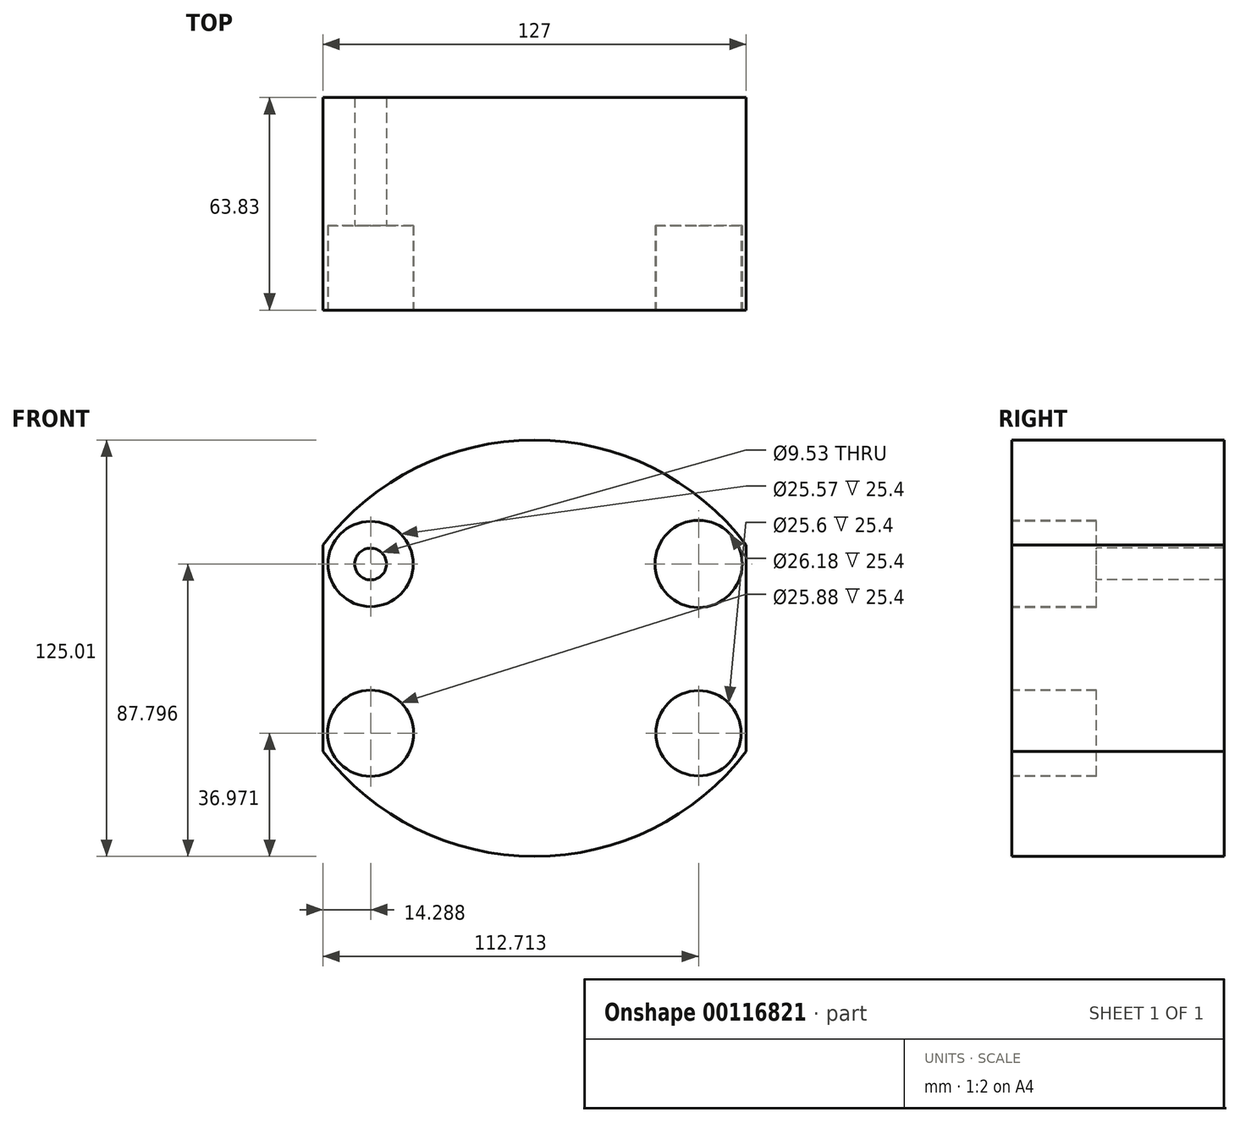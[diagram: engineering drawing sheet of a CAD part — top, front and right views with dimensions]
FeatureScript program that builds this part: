
annotation { "Feature Type Name" : "Feature", "Feature Type Description" : "" }
export const myFeature = defineFeature(function(context is Context, id is Id, definition is map)
    precondition{}
    {
        {
            var Q0;
            Q0=qCreatedBy(makeId("Front.planeOp"),FACE);
            var sketch = newSketch(context, id + "F0", { "sketchPlane" : qUnion([Q0])});
            skLineSegment(sketch, "E0.bottom", {"start": v(-63.5, 31) * mm, "end": v(63.5, 31) * mm});
            skLineSegment(sketch, "E0.top", {"start": v(-63.5, -31) * mm, "end": v(63.5, -31) * mm});
            skLineSegment(sketch, "E0.left", {"start": v(-63.5, 31) * mm, "end": v(-63.5, -31) * mm});
            skLineSegment(sketch, "E0.right", {"start": v(63.5, 31) * mm, "end": v(63.5, -31) * mm});
            skPoint(sketch, "E0.middle", {"position": v(0, 0) * mm});
            skLineSegment(sketch, "E1", {"start": v(0, 0) * mm, "end": v(0, -62.5) * mm});
            skLineSegment(sketch, "E2", {"start": v(0, -62.5) * mm, "end": v(0, 0) * mm});
            skLineSegment(sketch, "E3", {"start": v(0, 0) * mm, "end": v(0, 62.5) * mm});
            skLineSegment(sketch, "E4", {"start": v(0, 62.5) * mm, "end": v(0, 0) * mm});
            skArc(sketch, "E5", {"start": v(63.5, 31) * mm, "mid": v(0, 62.5) * mm, "end": v(-63.5, 31) * mm});
            skArc(sketch, "E6", {"start": v(-63.5, -31) * mm, "mid": v(0, -62.5) * mm, "end": v(63.5, -31) * mm});
            skSolve(sketch);
        }
        {
            var Q0;
            Q0=qSketchRegion(id+"F0",true);
            extrude(context, id + "F1", {"entities" : qUnion([Q0]), "depth" : 104.5 * mm});
        }
        {
            var Q0;
            Q0=makeQuery(id+"F1.opExtrude","SWEPT_FACE",FACE,{"disambiguationData":[OSD([sQuery(id+"F0.wireOp",EDGE,"E0.right")])]});
            var sketch = newSketch(context, id + "F2", { "sketchPlane" : qUnion([Q0])});
            skLineSegment(sketch, "E7.bottom", {"start": v(-104.5, 31) * mm, "end": v(-62.5, 31) * mm});
            skLineSegment(sketch, "E7.top", {"start": v(-104.5, -31) * mm, "end": v(-62.5, -31) * mm});
            skLineSegment(sketch, "E7.left", {"start": v(-104.5, 31) * mm, "end": v(-104.5, -31) * mm});
            skLineSegment(sketch, "E7.right", {"start": v(-62.5, 31) * mm, "end": v(-62.5, -31) * mm});
            skLineSegment(sketch, "E8", {"start": v(-62.5, 31) * mm, "end": v(-62.5, 64.33) * mm});
            skLineSegment(sketch, "E9", {"start": v(-62.5, 64.33) * mm, "end": v(-104.5, 31) * mm});
            skLineSegment(sketch, "E10", {"start": v(-62.5, -31) * mm, "end": v(-62.5, -65.1) * mm});
            skLineSegment(sketch, "E11", {"start": v(-62.5, -65.1) * mm, "end": v(-104.5, -31) * mm});
            skLineSegment(sketch, "E12", {"start": v(-104.5, -31) * mm, "end": v(-104.5, -67.31) * mm});
            skLineSegment(sketch, "E13", {"start": v(-104.5, -67.31) * mm, "end": v(-62.5, -65.1) * mm});
            skLineSegment(sketch, "E14", {"start": v(-104.5, 31) * mm, "end": v(-104.5, 72.84) * mm});
            skLineSegment(sketch, "E15", {"start": v(-104.5, 72.84) * mm, "end": v(-62.5, 64.33) * mm});
            skSolve(sketch);
        }
        {
            var Q0;
            Q0=makeQuery(id+"F2.imprint","IMPRINT",FACE,{"disambiguationData":[TD([[makeQuery(id+"F2.imprint","IMPRINT",EDGE,{"derivedFrom":sQuery(id+"F2.wireOp",EDGE,"E9")}),-1.0]])]});
            var Q1;
            Q1=makeQuery(id+"F2.imprint","IMPRINT",FACE,{"disambiguationData":[TD([[makeQuery(id+"F2.imprint","IMPRINT",EDGE,{"derivedFrom":sQuery(id+"F2.wireOp",EDGE,"E11")}),1.0]])]});
            extrude(context, id + "F3", {"entities" : qUnion([Q0, Q1]), "operationType" : NewBodyOperationType.REMOVE, "endBound" : BoundingType.THROUGH_ALL, "oppositeDirection" : true, "depth" : 25.4 * mm});
        }
        {
            var Q0;
            Q0=makeQuery(id+"F1.opExtrude","CAP_FACE",FACE,{"disambiguationData":[OSD([sQuery(id+"F0.wireOp",EDGE,"E0.left"),sQuery(id+"F0.wireOp",EDGE,"E0.right"),sQuery(id+"F0.wireOp",EDGE,"E5"),sQuery(id+"F0.wireOp",EDGE,"E6")])],"isStart":false});
            var sketch = newSketch(context, id + "F4", { "sketchPlane" : qUnion([Q0])});
            skLineSegment(sketch, "E16.bottom", {"start": v(-63.5, 31) * mm, "end": v(63.5, 31) * mm});
            skLineSegment(sketch, "E16.top", {"start": v(-63.5, -31) * mm, "end": v(63.5, -31) * mm});
            skLineSegment(sketch, "E16.left", {"start": v(-63.5, 31) * mm, "end": v(-63.5, -31) * mm});
            skLineSegment(sketch, "E16.right", {"start": v(63.5, 31) * mm, "end": v(63.5, -31) * mm});
            skSolve(sketch);
        }
        {
            var Q0;
            Q0=qSketchRegion(id+"F4",true);
            extrude(context, id + "F5", {"entities" : qUnion([Q0]), "operationType" : NewBodyOperationType.ADD, "depth" : 27 * mm});
        }
        {
            var Q0;
            Q0=makeQuery(id+"F5.opExtrude","SWEPT_FACE",FACE,{"disambiguationData":[OSD([sQuery(id+"F4.wireOp",EDGE,"E16.top")])]});
            var sketch = newSketch(context, id + "F6", { "sketchPlane" : qUnion([Q0])});
            skPoint(sketch, "E17", {"position": v(0, 131.5) * mm});
            skArc(sketch, "E18", {"start": v(63.5, 104.5) * mm, "mid": v(0, 131.5) * mm, "end": v(-63.5, 104.5) * mm});
            skLineSegment(sketch, "E19.bottom", {"start": v(-63.5, 131.5) * mm, "end": v(63.5, 131.5) * mm});
            skLineSegment(sketch, "E19.top", {"start": v(-63.5, 104.5) * mm, "end": v(63.5, 104.5) * mm});
            skLineSegment(sketch, "E19.left", {"start": v(-63.5, 131.5) * mm, "end": v(-63.5, 104.5) * mm});
            skLineSegment(sketch, "E19.right", {"start": v(63.5, 131.5) * mm, "end": v(63.5, 104.5) * mm});
            skSolve(sketch);
        }
        {
            var Q0;
            {var subQ0=sQuery(id+"F6.wireOp",EDGE,"E19.left");Q0=makeQuery(id+"F6.imprint","IMPRINT",FACE,{"disambiguationData":[TD([[makeQuery(id+"F6.imprint","IMPRINT",EDGE,{"derivedFrom":subQ0}),1.0]])]});}
            var Q1;
            {var subQ0=sQuery(id+"F6.wireOp",EDGE,"E19.right");Q1=makeQuery(id+"F6.imprint","IMPRINT",FACE,{"disambiguationData":[TD([[makeQuery(id+"F6.imprint","IMPRINT",EDGE,{"derivedFrom":subQ0}),-1.0]])]});}
            extrude(context, id + "F7", {"entities" : qUnion([Q0, Q1]), "operationType" : NewBodyOperationType.REMOVE, "endBound" : BoundingType.THROUGH_ALL, "oppositeDirection" : true, "depth" : 25.4 * mm});
        }
        {
            var Q0;
            Q0=makeQuery(id+"F5.boolean.opBoolean","MERGE",FACE,{"derivedFrom":[makeQuery(id+"F1.opExtrude","SWEPT_FACE",FACE,{"disambiguationData":[OSD([sQuery(id+"F0.wireOp",EDGE,"E0.right")])]}),makeQuery(id+"F5.opExtrude","SWEPT_FACE",FACE,{"disambiguationData":[OSD([sQuery(id+"F4.wireOp",EDGE,"E16.right")])]})]});
            var sketch = newSketch(context, id + "F8", { "sketchPlane" : qUnion([Q0])});
            skLineSegment(sketch, "E20.bottom", {"start": v(-142.12, -108.78) * mm, "end": v(-63.83, -108.78) * mm});
            skLineSegment(sketch, "E20.top", {"start": v(-142.12, 98.37) * mm, "end": v(-63.83, 98.37) * mm});
            skLineSegment(sketch, "E20.left", {"start": v(-142.12, -108.78) * mm, "end": v(-142.12, 98.37) * mm});
            skLineSegment(sketch, "E20.right", {"start": v(-63.83, -108.78) * mm, "end": v(-63.83, 98.37) * mm});
            skSolve(sketch);
        }
        {
            var Q0;
            Q0 = qSketchRegion(id + "F8", true);
            extrude(context, id + "F9", {"entities" : qUnion([Q0]), "operationType" : NewBodyOperationType.REMOVE, "endBound" : BoundingType.THROUGH_ALL, "oppositeDirection" : true, "depth" : 25.4 * mm});
        }
        {
            var Q0;
            Q0=makeQuery(id+"F9.boolean.opBoolean","COPY",FACE,{"derivedFrom":makeQuery(id+"F9.opExtrude","SWEPT_FACE",FACE,{"disambiguationData":[OSD([sQuery(id+"F8.wireOp",EDGE,"E20.right")])]})});
            var sketch = newSketch(context, id + "F10", { "sketchPlane" : qUnion([Q0])});
            skLineSegment(sketch, "E21", {"start": v(0, 0) * mm, "end": v(-49.21, 0) * mm});
            skLineSegment(sketch, "E22", {"start": v(-49.21, 0) * mm, "end": v(0, 0) * mm});
            skLineSegment(sketch, "E23", {"start": v(0, 0) * mm, "end": v(49.21, 0) * mm});
            skLineSegment(sketch, "E24", {"start": v(49.21, 0) * mm, "end": v(0, 0) * mm});
            skLineSegment(sketch, "E25", {"start": v(49.21, 0) * mm, "end": v(49.21, -25.53) * mm});
            skLineSegment(sketch, "E26", {"start": v(49.21, -25.53) * mm, "end": v(49.21, 25.3) * mm});
            skLineSegment(sketch, "E27", {"start": v(49.21, 25.3) * mm, "end": v(49.21, -25.53) * mm});
            skLineSegment(sketch, "E28", {"start": v(-49.21, 0) * mm, "end": v(-49.21, -25.53) * mm});
            skLineSegment(sketch, "E29", {"start": v(-49.21, -25.53) * mm, "end": v(-49.21, 25.3) * mm});
            skLineSegment(sketch, "E30", {"start": v(-49.21, 25.3) * mm, "end": v(49.21, 25.3) * mm});
            skLineSegment(sketch, "E31", {"start": v(49.21, -25.53) * mm, "end": v(-49.21, -25.53) * mm});
            skCircle(sketch, "E32", {"center": v(49.21, -25.53) * mm, "radius": 4.76 * mm});
            skCircle(sketch, "E33", {"center": v(-49.21, -25.53) * mm, "radius": 4.76 * mm});
            skCircle(sketch, "E34", {"center": v(49.21, 25.3) * mm, "radius": 4.76 * mm});
            skCircle(sketch, "E35", {"center": v(-49.21, 25.3) * mm, "radius": 4.76 * mm});
            skSolve(sketch);
        }
        {
            var Q0;
            {var subQ0=sQuery(id+"F10.wireOp",EDGE,"E31");var subQ1=sQuery(id+"F10.wireOp",EDGE,"E27");var subQ2=makeQuery(id+"F10.imprint","INTERSECT",VERTEX,{"derivedFrom":[subQ1,subQ0]});Q0=makeQuery(id+"F10.imprint","IMPRINT",FACE,{"disambiguationData":[TD([[makeQuery(id+"F10.imprint","IMPRINT",EDGE,{"disambiguationData":[TD([[subQ2,1.0]])],"derivedFrom":subQ1}),1.0]])]});}
            var Q1;
            {var subQ0=sQuery(id+"F10.wireOp",EDGE,"E31");var subQ1=sQuery(id+"F10.wireOp",EDGE,"E27");var subQ2=makeQuery(id+"F10.imprint","INTERSECT",VERTEX,{"derivedFrom":[subQ1,subQ0]});Q1=makeQuery(id+"F10.imprint","IMPRINT",FACE,{"disambiguationData":[TD([[makeQuery(id+"F10.imprint","IMPRINT",EDGE,{"disambiguationData":[TD([[subQ2,1.0]])],"derivedFrom":subQ1}),-1.0]])]});}
            var Q2;
            {var subQ0=sQuery(id+"F10.wireOp",EDGE,"E31");var subQ1=sQuery(id+"F10.wireOp",EDGE,"E29");var subQ2=makeQuery(id+"F10.imprint","INTERSECT",VERTEX,{"derivedFrom":[subQ1,subQ0]});Q2=makeQuery(id+"F10.imprint","IMPRINT",FACE,{"disambiguationData":[TD([[makeQuery(id+"F10.imprint","IMPRINT",EDGE,{"disambiguationData":[TD([[subQ2,-1.0]])],"derivedFrom":subQ1}),-1.0]])]});}
            var Q3;
            {var subQ0=sQuery(id+"F10.wireOp",EDGE,"E31");var subQ1=sQuery(id+"F10.wireOp",EDGE,"E29");var subQ2=makeQuery(id+"F10.imprint","INTERSECT",VERTEX,{"derivedFrom":[subQ1,subQ0]});Q3=makeQuery(id+"F10.imprint","IMPRINT",FACE,{"disambiguationData":[TD([[makeQuery(id+"F10.imprint","IMPRINT",EDGE,{"disambiguationData":[TD([[subQ2,-1.0]])],"derivedFrom":subQ1}),1.0]])]});}
            var Q4;
            {var subQ0=sQuery(id+"F10.wireOp",EDGE,"E30");var subQ1=sQuery(id+"F10.wireOp",EDGE,"E29");var subQ2=makeQuery(id+"F10.imprint","INTERSECT",VERTEX,{"derivedFrom":[subQ1,subQ0]});Q4=makeQuery(id+"F10.imprint","IMPRINT",FACE,{"disambiguationData":[TD([[makeQuery(id+"F10.imprint","IMPRINT",EDGE,{"disambiguationData":[TD([[subQ2,1.0]])],"derivedFrom":subQ1}),1.0]])]});}
            var Q5;
            {var subQ0=sQuery(id+"F10.wireOp",EDGE,"E30");var subQ1=sQuery(id+"F10.wireOp",EDGE,"E29");var subQ2=makeQuery(id+"F10.imprint","INTERSECT",VERTEX,{"derivedFrom":[subQ1,subQ0]});Q5=makeQuery(id+"F10.imprint","IMPRINT",FACE,{"disambiguationData":[TD([[makeQuery(id+"F10.imprint","IMPRINT",EDGE,{"disambiguationData":[TD([[subQ2,1.0]])],"derivedFrom":subQ1}),-1.0]])]});}
            var Q6;
            {var subQ0=sQuery(id+"F10.wireOp",EDGE,"E30");var subQ1=sQuery(id+"F10.wireOp",EDGE,"E27");var subQ2=makeQuery(id+"F10.imprint","INTERSECT",VERTEX,{"derivedFrom":[subQ1,subQ0]});Q6=makeQuery(id+"F10.imprint","IMPRINT",FACE,{"disambiguationData":[TD([[makeQuery(id+"F10.imprint","IMPRINT",EDGE,{"disambiguationData":[TD([[subQ2,-1.0]])],"derivedFrom":subQ1}),1.0]])]});}
            var Q7;
            {var subQ0=sQuery(id+"F10.wireOp",EDGE,"E30");var subQ1=sQuery(id+"F10.wireOp",EDGE,"E27");var subQ2=makeQuery(id+"F10.imprint","INTERSECT",VERTEX,{"derivedFrom":[subQ1,subQ0]});Q7=makeQuery(id+"F10.imprint","IMPRINT",FACE,{"disambiguationData":[TD([[makeQuery(id+"F10.imprint","IMPRINT",EDGE,{"disambiguationData":[TD([[subQ2,-1.0]])],"derivedFrom":subQ1}),-1.0]])]});}
            extrude(context, id + "F11", {"entities" : qUnion([Q0, Q1, Q2, Q3, Q4, Q5, Q6, Q7]), "operationType" : NewBodyOperationType.REMOVE, "endBound" : BoundingType.THROUGH_ALL, "oppositeDirection" : true, "depth" : 25.4 * mm});
        }
        {
            var Q0;
            Q0=makeQuery(id+"F9.boolean.opBoolean","COPY",FACE,{"derivedFrom":makeQuery(id+"F9.opExtrude","SWEPT_FACE",FACE,{"disambiguationData":[OSD([sQuery(id+"F8.wireOp",EDGE,"E20.right")])]})});
            var sketch = newSketch(context, id + "F12", { "sketchPlane" : qUnion([Q0])});
            skCircle(sketch, "E36", {"center": v(49.21, -25.53) * mm, "radius": 12.8 * mm});
            skCircle(sketch, "E37", {"center": v(-49.21, -25.53) * mm, "radius": 12.94 * mm});
            skCircle(sketch, "E38", {"center": v(-49.21, 25.3) * mm, "radius": 12.78 * mm});
            skCircle(sketch, "E39", {"center": v(49.21, 25.3) * mm, "radius": 13.09 * mm});
            skSolve(sketch);
        }
        {
            var Q0;
            Q0 = qSketchRegion(id + "F12", true);
            extrude(context, id + "F13", {"entities" : qUnion([Q0]), "operationType" : NewBodyOperationType.REMOVE, "oppositeDirection" : true, "depth" : 25.4 * mm});
        }
    });
